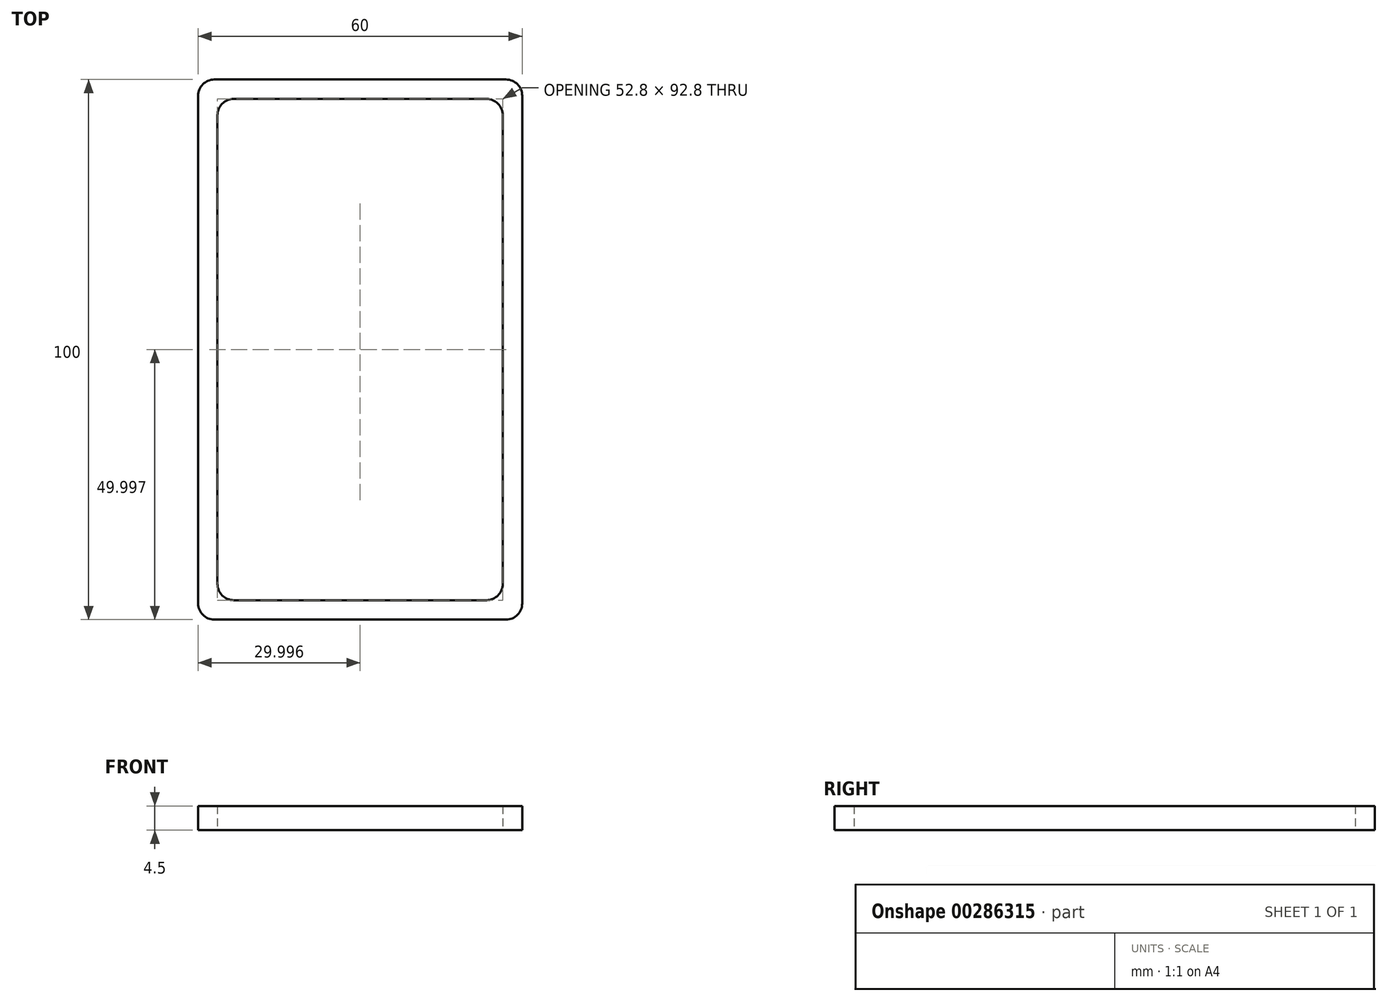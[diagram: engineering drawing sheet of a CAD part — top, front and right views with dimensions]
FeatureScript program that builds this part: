
annotation { "Feature Type Name" : "Feature", "Feature Type Description" : "" }
export const myFeature = defineFeature(function(context is Context, id is Id, definition is map)
    precondition{}
    {
        {
            var Q0;
            Q0=qCreatedBy(makeId("Top.planeOp"),FACE);
            var sketch = newSketch(context, id + "F0", { "sketchPlane" : qUnion([Q0])});
            skLineSegment(sketch, "E0", {"start": v(-38.54, 54) * mm, "end": v(15.46, 54) * mm});
            skLineSegment(sketch, "E1", {"start": v(18.46, 51) * mm, "end": v(18.46, -43) * mm});
            skLineSegment(sketch, "E2", {"start": v(15.46, -46) * mm, "end": v(-38.54, -46) * mm});
            skLineSegment(sketch, "E3", {"start": v(-41.54, -43) * mm, "end": v(-41.54, 51) * mm});
            skLineSegment(sketch, "E4", {"start": v(-41.54, 5.96) * mm, "end": v(-37.94, 5.96) * mm});
            skLineSegment(sketch, "E5", {"start": v(-11.54, -46) * mm, "end": v(-11.54, -42.4) * mm});
            skLineSegment(sketch, "E6", {"start": v(18.46, -7.23) * mm, "end": v(14.86, -7.23) * mm});
            skLineSegment(sketch, "E7", {"start": v(-11.54, 54) * mm, "end": v(-11.54, 50.4) * mm});
            skLineSegment(sketch, "E8", {"start": v(-34.94, 50.4) * mm, "end": v(11.86, 50.4) * mm});
            skLineSegment(sketch, "E9", {"start": v(14.86, 47.4) * mm, "end": v(14.86, -39.4) * mm});
            skLineSegment(sketch, "E10", {"start": v(11.86, -42.4) * mm, "end": v(-34.94, -42.4) * mm});
            skLineSegment(sketch, "E11", {"start": v(-37.94, -39.4) * mm, "end": v(-37.94, 47.4) * mm});
            skPoint(sketch, "E12.visualSharp", {"position": v(-41.54, 54) * mm});
            skArc(sketch, "E12.filletArc", {"start": v(-38.54, 54) * mm, "mid": v(-40.66, 53.13) * mm, "end": v(-41.54, 51) * mm});
            skPoint(sketch, "E13.visualSharp", {"position": v(18.46, 54) * mm});
            skArc(sketch, "E13.filletArc", {"start": v(18.46, 51) * mm, "mid": v(17.58, 53.13) * mm, "end": v(15.46, 54) * mm});
            skPoint(sketch, "E14.visualSharp", {"position": v(18.46, -46) * mm});
            skArc(sketch, "E14.filletArc", {"start": v(15.46, -46) * mm, "mid": v(17.58, -45.11) * mm, "end": v(18.46, -43) * mm});
            skPoint(sketch, "E15.visualSharp", {"position": v(-41.54, -46) * mm});
            skArc(sketch, "E15.filletArc", {"start": v(-41.54, -43) * mm, "mid": v(-40.66, -45.11) * mm, "end": v(-38.54, -46) * mm});
            skPoint(sketch, "E16.visualSharp", {"position": v(-37.94, -42.4) * mm});
            skArc(sketch, "E16.filletArc", {"start": v(-37.94, -39.4) * mm, "mid": v(-37.06, -41.51) * mm, "end": v(-34.94, -42.4) * mm});
            skPoint(sketch, "E17.visualSharp", {"position": v(14.86, 50.4) * mm});
            skArc(sketch, "E17.filletArc", {"start": v(14.86, 47.4) * mm, "mid": v(13.98, 49.53) * mm, "end": v(11.86, 50.4) * mm});
            skPoint(sketch, "E18.visualSharp", {"position": v(-37.94, 50.4) * mm});
            skArc(sketch, "E18.filletArc", {"start": v(-34.94, 50.4) * mm, "mid": v(-37.06, 49.53) * mm, "end": v(-37.94, 47.4) * mm});
            skPoint(sketch, "E19.visualSharp", {"position": v(14.86, -42.4) * mm});
            skArc(sketch, "E19.filletArc", {"start": v(11.86, -42.4) * mm, "mid": v(13.98, -41.51) * mm, "end": v(14.86, -39.4) * mm});
            skSolve(sketch);
        }
        {
            var Q0;
            {var subQ1=sQuery(id+"F0.wireOp",EDGE,"E5");Q0=makeQuery(id+"F0.imprint","IMPRINT",FACE,{"disambiguationData":[TD([[makeQuery(id+"F0.imprint","IMPRINT",EDGE,{"derivedFrom":subQ1}),-1.0]])]});}
            var Q1;
            {var subQ1=sQuery(id+"F0.wireOp",EDGE,"E4");Q1=makeQuery(id+"F0.imprint","IMPRINT",FACE,{"disambiguationData":[TD([[makeQuery(id+"F0.imprint","IMPRINT",EDGE,{"derivedFrom":subQ1}),-1.0]])]});}
            var Q2;
            {var subQ0=sQuery(id+"F0.wireOp",EDGE,"E6");Q2=makeQuery(id+"F0.imprint","IMPRINT",FACE,{"disambiguationData":[TD([[makeQuery(id+"F0.imprint","IMPRINT",EDGE,{"derivedFrom":subQ0}),-1.0]])]});}
            var Q3;
            {var subQ3=sQuery(id+"F0.wireOp",EDGE,"E4");Q3=makeQuery(id+"F0.imprint","IMPRINT",FACE,{"disambiguationData":[TD([[makeQuery(id+"F0.imprint","IMPRINT",EDGE,{"derivedFrom":subQ3}),1.0]])]});}
            extrude(context, id + "F1", {"entities" : qUnion([Q0, Q1, Q2, Q3]), "depth" : 4.5 * mm});
        }
    });
